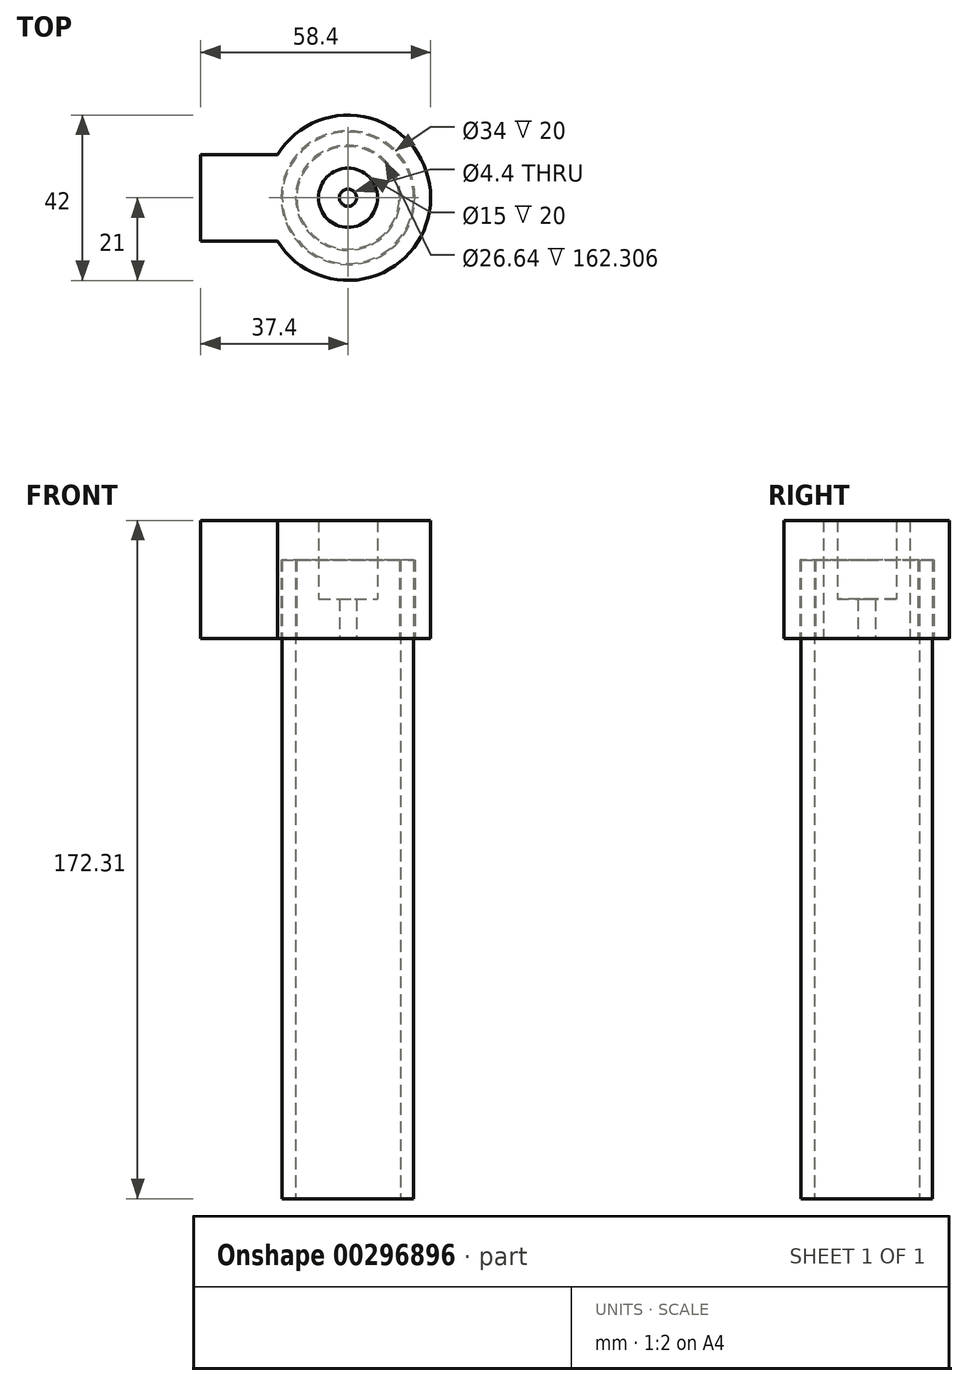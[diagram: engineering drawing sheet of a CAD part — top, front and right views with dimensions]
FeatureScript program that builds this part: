
annotation { "Feature Type Name" : "Feature", "Feature Type Description" : "" }
export const myFeature = defineFeature(function(context is Context, id is Id, definition is map)
    precondition{}
    {
        {
            var Q0;
            Q0=qCreatedBy(makeId("Top.planeOp"),FACE);
            var sketch = newSketch(context, id + "F0", { "sketchPlane" : qUnion([Q0])});
            skCircle(sketch, "E0", {"center": v(0, 0) * mm, "radius": 16.7 * mm});
            skCircle(sketch, "E1", {"center": v(0, 0) * mm, "radius": 13.32 * mm});
            skSolve(sketch);
        }
        {
            var Q0;
            Q0 = qSketchRegion(id + "F0", true);
            extrude(context, id + "F1", {"entities" : qUnion([Q0]), "depth" : 162.3 * mm});
        }
        {
            var Q0;
            Q0=qCreatedBy(makeId("Front.planeOp"),FACE);
            var sketch = newSketch(context, id + "F2", { "sketchPlane" : qUnion([Q0])});
            skLineSegment(sketch, "E2", {"start": v(-17, 142.3) * mm, "end": v(-17, 162.3) * mm});
            skLineSegment(sketch, "E3", {"start": v(-17, 162.3) * mm, "end": v(-13.02, 162.3) * mm});
            skLineSegment(sketch, "E4", {"start": v(-13.02, 162.3) * mm, "end": v(-13.02, 142.3) * mm});
            skLineSegment(sketch, "E5", {"start": v(-13.02, 142.3) * mm, "end": v(-2.2, 142.3) * mm});
            skLineSegment(sketch, "E6", {"start": v(-2.2, 142.3) * mm, "end": v(-2.2, 152.3) * mm});
            skLineSegment(sketch, "E7", {"start": v(-7.5, 172.3) * mm, "end": v(-21, 172.3) * mm});
            skLineSegment(sketch, "E8", {"start": v(-21, 172.3) * mm, "end": v(-21, 142.3) * mm});
            skLineSegment(sketch, "E9", {"start": v(-21, 142.3) * mm, "end": v(-17, 142.3) * mm});
            skLineSegment(sketch, "E10", {"start": v(-13.02, 0) * mm, "end": v(-13.02, 142.3) * mm, "construction": true});
            skLineSegment(sketch, "E11", {"start": v(-17, 142.3) * mm, "end": v(-17, 0) * mm, "construction": true});
            skLineSegment(sketch, "E12", {"start": v(-17, 0) * mm, "end": v(-13.02, 0) * mm, "construction": true});
            skLineSegment(sketch, "E13", {"start": v(0, 0) * mm, "end": v(-7, 0) * mm, "construction": true});
            skLineSegment(sketch, "E14", {"start": v(0, 0) * mm, "end": v(7, 0) * mm, "construction": true});
            skLineSegment(sketch, "E15", {"start": v(-7, 0) * mm, "end": v(-7, 207.88) * mm, "construction": true});
            skLineSegment(sketch, "E16", {"start": v(-7, 207.88) * mm, "end": v(7, 207.88) * mm, "construction": true});
            skLineSegment(sketch, "E17", {"start": v(7, 207.88) * mm, "end": v(7, 0) * mm, "construction": true});
            skLineSegment(sketch, "E18", {"start": v(0, 0) * mm, "end": v(0, 207.88) * mm, "construction": true});
            skLineSegment(sketch, "E19", {"start": v(-2.2, 152.3) * mm, "end": v(-7.5, 152.3) * mm});
            skLineSegment(sketch, "E20", {"start": v(-7.5, 152.3) * mm, "end": v(-7.5, 172.3) * mm});
            skSolve(sketch);
        }
        {
            var Q0;
            Q0=makeQuery(id+"F2.imprint","IMPRINT",FACE,{"disambiguationData":[TD([[makeQuery(id+"F2.imprint","IMPRINT",EDGE,{"derivedFrom":sQuery(id+"F2.wireOp",EDGE,"E2")}),1.0]])]});
            var Q1;
            Q1=sQuery(id+"F2.wireOp",EDGE,"E18");
            revolve(context, id + "F3", {"entities" : qUnion([Q0]), "axis" : qUnion([Q1]), "revolveType" : RevolveType.FULL});
        }
        {
            var Q0;
            Q0=qCreatedBy(makeId("Right.planeOp"),FACE);
            cPlane(context, id + "F4", {"entities" : qUnion([Q0]), "cplaneType" : CPlaneType.OFFSET, "offset" : 17.4 * mm, "oppositeDirection" : true, "width" : 150 * mm, "height" : 150 * mm});
        }
        {
            var Q0;
            Q0=qCreatedBy(id+"F4.planeOp",FACE);
            var sketch = newSketch(context, id + "F5", { "sketchPlane" : qUnion([Q0])});
            skLineSegment(sketch, "E21.bottom", {"start": v(11, 172.3) * mm, "end": v(-11, 172.3) * mm});
            skLineSegment(sketch, "E21.top", {"start": v(11, 142.3) * mm, "end": v(-11, 142.3) * mm});
            skLineSegment(sketch, "E21.left", {"start": v(11, 172.3) * mm, "end": v(11, 142.3) * mm});
            skLineSegment(sketch, "E21.right", {"start": v(-11, 172.3) * mm, "end": v(-11, 142.3) * mm});
            skLineSegment(sketch, "E22", {"start": v(0, 142.3) * mm, "end": v(0, 172.3) * mm, "construction": true});
            skLineSegment(sketch, "E23", {"start": v(0, 142.3) * mm, "end": v(0, 5.2) * mm, "construction": true});
            skSolve(sketch);
        }
        {
            var Q0;
            Q0 = qSketchRegion(id + "F5", true);
            extrude(context, id + "F6", {"entities" : qUnion([Q0]), "operationType" : NewBodyOperationType.ADD, "oppositeDirection" : true, "depth" : 20 * mm});
        }
    });
